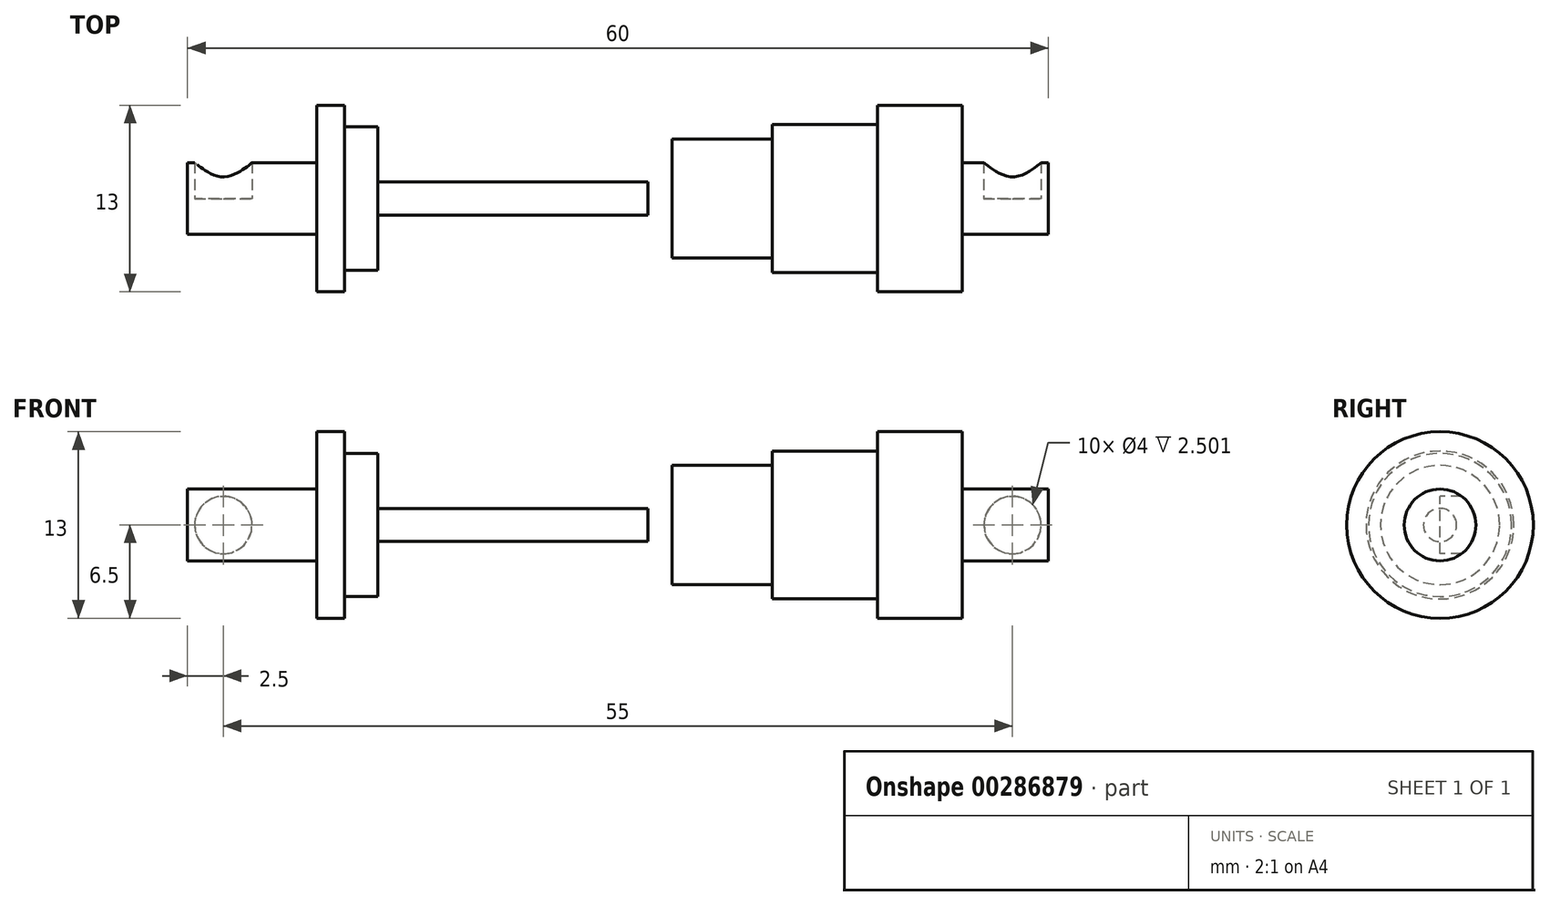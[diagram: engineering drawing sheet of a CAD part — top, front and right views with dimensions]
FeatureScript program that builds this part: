
annotation { "Feature Type Name" : "Feature", "Feature Type Description" : "" }
export const myFeature = defineFeature(function(context is Context, id is Id, definition is map)
    precondition{}
    {
        {
            var Q0;
            Q0=qCreatedBy(makeId("Front.planeOp"),FACE);
            var sketch = newSketch(context, id + "F0", { "sketchPlane" : qUnion([Q0])});
            skLineSegment(sketch, "E0", {"start": v(-30, 0) * mm, "end": v(2.1, 0) * mm});
            skLineSegment(sketch, "E1", {"start": v(-30, 2.5) * mm, "end": v(-30, 0) * mm});
            skLineSegment(sketch, "E2", {"start": v(30, 2.5) * mm, "end": v(30, 0) * mm});
            skLineSegment(sketch, "E3", {"start": v(30, 2.5) * mm, "end": v(24, 2.5) * mm});
            skPoint(sketch, "E4.orphan", {"position": v(30, -2.5) * mm});
            skPoint(sketch, "E5.orphan", {"position": v(-30, -2.5) * mm});
            skLineSegment(sketch, "E6", {"start": v(24, 2.5) * mm, "end": v(24, 6.5) * mm});
            skLineSegment(sketch, "E7", {"start": v(24, 6.5) * mm, "end": v(18.09, 6.5) * mm});
            skLineSegment(sketch, "E8", {"start": v(-21, 6.5) * mm, "end": v(-21, 2.5) * mm});
            skLineSegment(sketch, "E9", {"start": v(-21, 2.5) * mm, "end": v(-30, 2.5) * mm});
            skLineSegment(sketch, "E10", {"start": v(18.09, 6.5) * mm, "end": v(18.09, 5.15) * mm});
            skLineSegment(sketch, "E11", {"start": v(18.09, 5.15) * mm, "end": v(10.76, 5.15) * mm});
            skLineSegment(sketch, "E12", {"start": v(10.76, 5.15) * mm, "end": v(10.76, 4.15) * mm});
            skLineSegment(sketch, "E13", {"start": v(10.76, 4.15) * mm, "end": v(3.76, 4.15) * mm});
            skLineSegment(sketch, "E14", {"start": v(3.76, 4.15) * mm, "end": v(3.76, 0) * mm});
            skLineSegment(sketch, "E15", {"start": v(-19.07, 6.5) * mm, "end": v(-19.07, 4.99) * mm});
            skLineSegment(sketch, "E16", {"start": v(-19.07, 4.99) * mm, "end": v(-16.73, 4.99) * mm});
            skLineSegment(sketch, "E17", {"start": v(-16.73, 4.99) * mm, "end": v(-16.73, 1.16) * mm});
            skLineSegment(sketch, "E18", {"start": v(-16.73, 1.16) * mm, "end": v(2.1, 1.16) * mm});
            skLineSegment(sketch, "E19", {"start": v(2.1, 1.16) * mm, "end": v(2.1, 0) * mm});
            skLineSegment(sketch, "E20.trimOffspring", {"start": v(-19.07, 6.5) * mm, "end": v(-21, 6.5) * mm});
            skLineSegment(sketch, "E21.trimOffspring", {"start": v(3.76, 0) * mm, "end": v(30, 0) * mm});
            skSolve(sketch);
        }
        {
            var Q0;
            Q0 = qSketchRegion(id + "F0", true);
            var Q1;
            Q1=sQuery(id+"F0.wireOp",EDGE,"E0");
            revolve(context, id + "F1", {"entities" : qUnion([Q0]), "axis" : qUnion([Q1]), "revolveType" : RevolveType.FULL});
        }
        {
            var Q0;
            Q0=qCreatedBy(makeId("Front.planeOp"),FACE);
            var sketch = newSketch(context, id + "F2", { "sketchPlane" : qUnion([Q0])});
            skCircle(sketch, "E22", {"center": v(27.5, 0) * mm, "radius": 2 * mm});
            skLineSegment(sketch, "E23", {"start": v(0, 0) * mm, "end": v(0, 10.88) * mm, "construction": true});
            skCircle(sketch, "E24.MirrorC", {"center": v(-27.5, 0) * mm, "radius": 2 * mm});
            skSolve(sketch);
        }
        {
            var Q0;
            Q0 = qSketchRegion(id + "F2", true);
            extrude(context, id + "F3", {"entities" : qUnion([Q0]), "operationType" : NewBodyOperationType.REMOVE, "endBound" : BoundingType.THROUGH_ALL, "oppositeDirection" : true, "depth" : 25 * mm});
        }
    });
